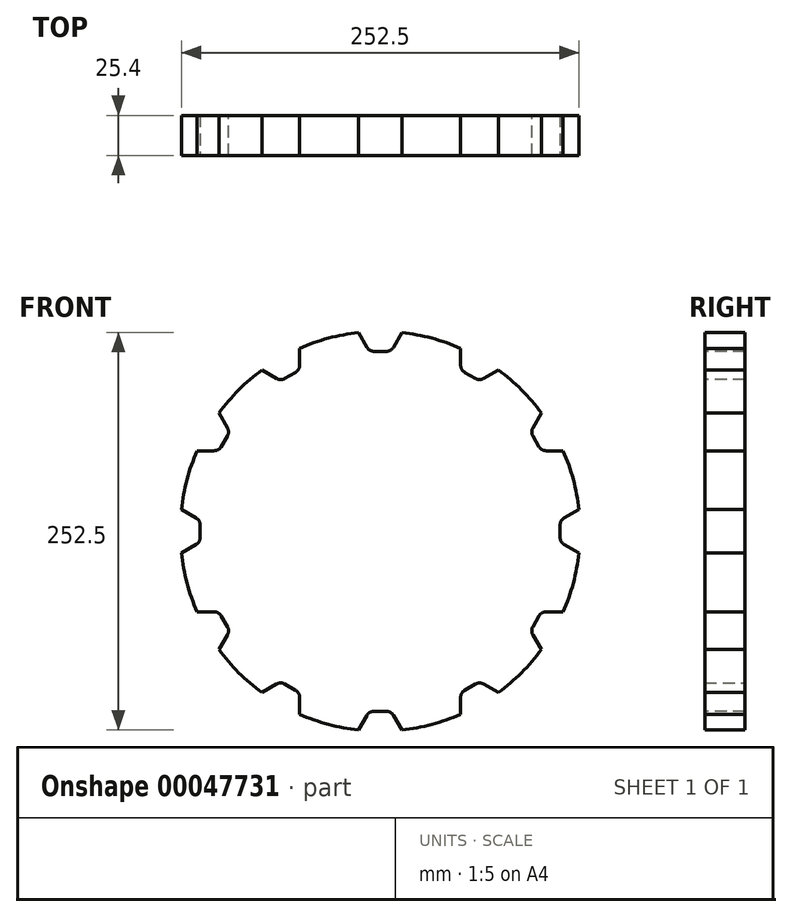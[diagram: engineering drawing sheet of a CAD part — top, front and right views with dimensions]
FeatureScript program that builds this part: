
annotation { "Feature Type Name" : "Feature", "Feature Type Description" : "" }
export const myFeature = defineFeature(function(context is Context, id is Id, definition is map)
    precondition{}
    {
        {
            var Q0;
            Q0=qCreatedBy(makeId("Front.planeOp"),FACE);
            var sketch = newSketch(context, id + "F0", { "sketchPlane" : qUnion([Q0])});
            skCircle(sketch, "E0", {"center": v(0, 0) * mm, "radius": 127 * mm});
            skSolve(sketch);
        }
        {
            var Q0;
            Q0=makeQuery(id+"F0.imprint","IMPRINT",FACE,{"disambiguationData":[TD([[makeQuery(id+"F0.imprint","IMPRINT",EDGE,{"derivedFrom":sQuery(id+"F0.wireOp",EDGE,"E0")}),1.0]])]});
            extrude(context, id + "F1", {"entities" : qUnion([Q0]), "endBound" : BoundingType.SYMMETRIC, "depth" : 25.4 * mm});
        }
        {
            var Q0;
            Q0=qCreatedBy(makeId("Front.planeOp"),FACE);
            var sketch = newSketch(context, id + "F2", { "sketchPlane" : qUnion([Q0])});
            skLineSegment(sketch, "E1", {"start": v(0, 0) * mm, "end": v(0, 127) * mm, "construction": true});
            skLineSegment(sketch, "E2", {"start": v(6.9, 114.3) * mm, "end": v(13.8, 126.25) * mm});
            skArc(sketch, "E3.0", {"start": v(13.8, 126.25) * mm, "mid": v(0, 127) * mm, "end": v(-13.8, 126.25) * mm});
            skLineSegment(sketch, "E4", {"start": v(6.9, 114.3) * mm, "end": v(0, 114.3) * mm});
            skPoint(sketch, "E5.orphan", {"position": v(0, 102.35) * mm});
            skLineSegment(sketch, "E6.MirrorCS", {"start": v(-6.9, 114.3) * mm, "end": v(-13.8, 126.25) * mm});
            skLineSegment(sketch, "E7.MirrorCS", {"start": v(-6.9, 114.3) * mm, "end": v(0, 114.3) * mm});
            skCircle(sketch, "E8", {"center": v(0, 0) * mm, "radius": 105.85 * mm, "construction": true});
            skSolve(sketch);
        }
        {
            var Q0;
            Q0=makeQuery(id+"F2.imprint","IMPRINT",FACE,{"disambiguationData":[TD([[makeQuery(id+"F2.imprint","IMPRINT",EDGE,{"derivedFrom":sQuery(id+"F2.wireOp",EDGE,"E2")}),1.0]])]});
            extrude(context, id + "F3", {"entities" : qUnion([Q0]), "operationType" : NewBodyOperationType.REMOVE, "endBound" : BoundingType.THROUGH_ALL, "oppositeDirection" : true, "depth" : 25.4 * mm, "hasSecondDirection" : true, "secondDirectionBound" : SecondDirectionBoundingType.THROUGH_ALL, "secondDirectionOppositeDirection" : false, "secondDirectionDepth" : 25.4 * mm});
        }
        {
            var Q0;
            Q0=makeQuery(id+"F3.boolean.opBoolean","COPY",EDGE,{"derivedFrom":makeQuery(id+"F3.opExtrude","SWEPT_EDGE",EDGE,{"disambiguationData":[OSD([sQuery(id+"F2.wireOp",EDGE,"E2"),sQuery(id+"F2.wireOp",EDGE,"E3.0")])]})});
            var Q1;
            Q1=makeQuery(id+"F3.boolean.opBoolean","COPY",EDGE,{"derivedFrom":makeQuery(id+"F3.opExtrude","SWEPT_EDGE",EDGE,{"disambiguationData":[OSD([sQuery(id+"F2.wireOp",EDGE,"E2"),sQuery(id+"F2.wireOp",EDGE,"E4")])]})});
            var Q2;
            Q2=makeQuery(id+"F3.boolean.opBoolean","COPY",EDGE,{"derivedFrom":makeQuery(id+"F3.opExtrude","SWEPT_EDGE",EDGE,{"disambiguationData":[OSD([sQuery(id+"F2.wireOp",EDGE,"E6.MirrorCS"),sQuery(id+"F2.wireOp",EDGE,"E7.MirrorCS")])]})});
            var Q3;
            Q3=makeQuery(id+"F3.boolean.opBoolean","COPY",EDGE,{"derivedFrom":makeQuery(id+"F3.opExtrude","SWEPT_EDGE",EDGE,{"disambiguationData":[OSD([sQuery(id+"F2.wireOp",EDGE,"E3.0"),sQuery(id+"F2.wireOp",EDGE,"E6.MirrorCS")])]})});
            fillet(context, id + "F4", {"entities" : qUnion([Q0, Q1, Q2, Q3]), "radius" : 5.08 * mm, "tangentPropagation" : true, "allowEdgeOverflow" : false});
        }
        {
            var Q0;
            Q0=makeQuery(id+"F4.opFillet","BLEND_FACE",FACE,{"disambiguationData":[OSD([sQuery(id+"F2.wireOp",EDGE,"E2"),sQuery(id+"F2.wireOp",EDGE,"E3.0")])]});
            var Q1;
            Q1=makeQuery(id+"F3.boolean.opBoolean","COPY",FACE,{"derivedFrom":makeQuery(id+"F3.opExtrude","SWEPT_FACE",FACE,{"disambiguationData":[OSD([sQuery(id+"F2.wireOp",EDGE,"E2")])]})});
            var Q2;
            Q2=makeQuery(id+"F4.opFillet","BLEND_FACE",FACE,{"disambiguationData":[OSD([sQuery(id+"F2.wireOp",EDGE,"E2"),sQuery(id+"F2.wireOp",EDGE,"E4")])]});
            var Q3;
            Q3=makeQuery(id+"F3.boolean.opBoolean","COPY",FACE,{"derivedFrom":makeQuery(id+"F3.opExtrude","SWEPT_FACE",FACE,{"disambiguationData":[OSD([sQuery(id+"F2.wireOp",EDGE,"E4"),sQuery(id+"F2.wireOp",EDGE,"E7.MirrorCS")])]})});
            var Q4;
            Q4=makeQuery(id+"F4.opFillet","BLEND_FACE",FACE,{"disambiguationData":[OSD([sQuery(id+"F2.wireOp",EDGE,"E6.MirrorCS"),sQuery(id+"F2.wireOp",EDGE,"E7.MirrorCS")])]});
            var Q5;
            Q5=makeQuery(id+"F3.boolean.opBoolean","COPY",FACE,{"derivedFrom":makeQuery(id+"F3.opExtrude","SWEPT_FACE",FACE,{"disambiguationData":[OSD([sQuery(id+"F2.wireOp",EDGE,"E6.MirrorCS")])]})});
            var Q6;
            Q6=makeQuery(id+"F4.opFillet","BLEND_FACE",FACE,{"disambiguationData":[OSD([sQuery(id+"F2.wireOp",EDGE,"E3.0"),sQuery(id+"F2.wireOp",EDGE,"E6.MirrorCS")])]});
            var Q7;
            Q7=sQuery(id+"F2.wireOp",EDGE,"E8");
            circularPattern(context, id + "F5", {"faces" : qUnion([Q0, Q1, Q2, Q3, Q4, Q5, Q6]), "axis" : qUnion([Q7]), "angle" : 30 * degree, "instanceCount" : 12, "patternType" : PatternType.FACE});
        }
    });
